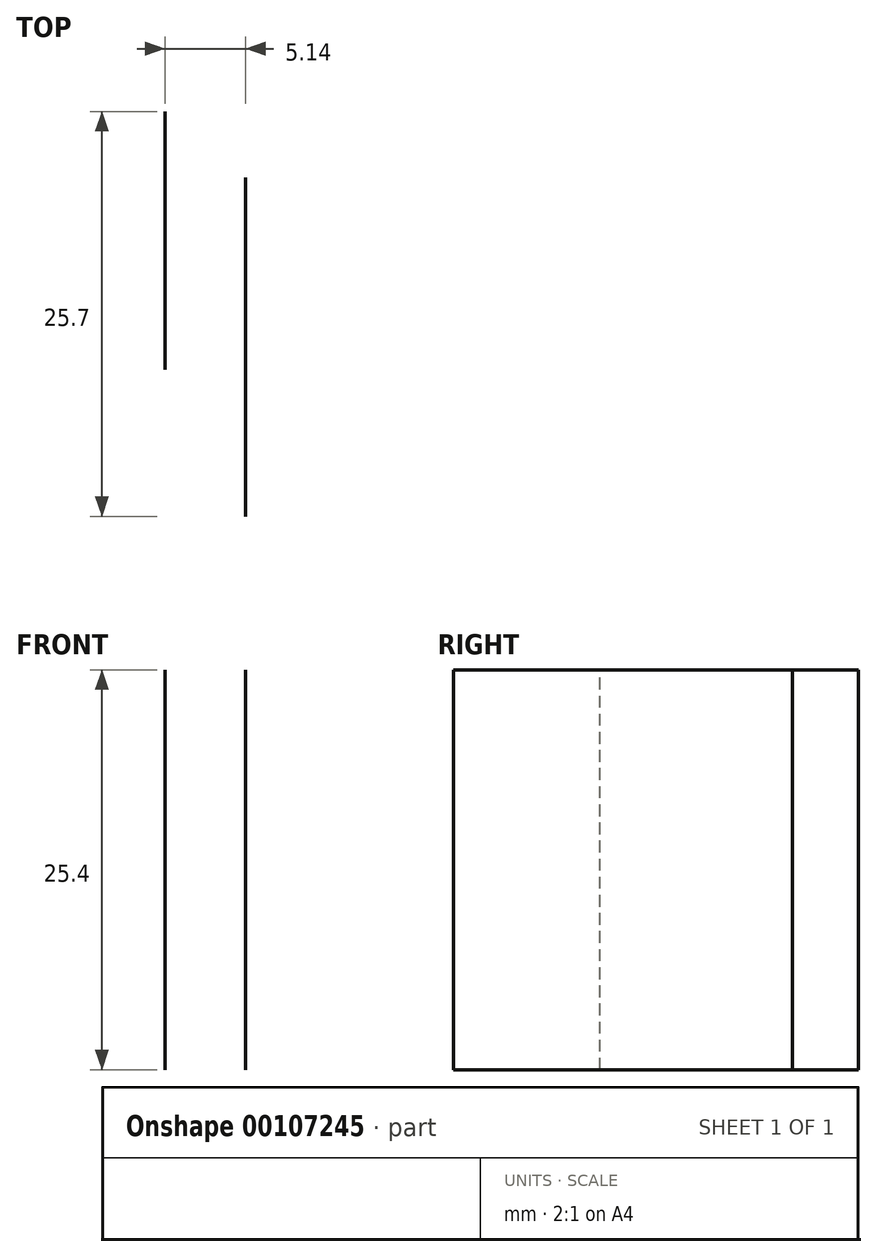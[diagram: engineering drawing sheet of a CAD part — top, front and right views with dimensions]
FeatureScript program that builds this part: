
annotation { "Feature Type Name" : "Feature", "Feature Type Description" : "" }
export const myFeature = defineFeature(function(context is Context, id is Id, definition is map)
    precondition{}
    {
        {
            var Q0;
            Q0=qCreatedBy(makeId("Top.planeOp"),FACE);
            var sketch = newSketch(context, id + "F0", { "sketchPlane" : qUnion([Q0])});
            skLineSegment(sketch, "E0.bottom", {"start": v(-113.75, 29.56) * mm, "end": v(112.79, 29.56) * mm});
            skLineSegment(sketch, "E0.top", {"start": v(-113.75, -33.42) * mm, "end": v(112.79, -33.42) * mm});
            skLineSegment(sketch, "E0.left", {"start": v(-113.75, 29.56) * mm, "end": v(-113.75, -33.42) * mm});
            skLineSegment(sketch, "E0.right", {"start": v(112.79, 29.56) * mm, "end": v(112.79, -33.42) * mm});
            skLineSegment(sketch, "E1", {"start": v(-27, 22.81) * mm, "end": v(-27, 6.43) * mm});
            skLineSegment(sketch, "E2", {"start": v(-21.85, 18.64) * mm, "end": v(-21.85, -2.9) * mm});
            skSolve(sketch);
        }
        {
            var Q0;
            Q0=qCreatedBy(makeId("Top.planeOp"),FACE);
            var sketch = newSketch(context, id + "F1", { "sketchPlane" : qUnion([Q0])});
            skLineSegment(sketch, "E3.0", {"start": v(-27, 22.81) * mm, "end": v(-27, 6.43) * mm});
            skLineSegment(sketch, "E4.0", {"start": v(-21.85, 18.64) * mm, "end": v(-21.85, -2.9) * mm});
            skLineSegment(sketch, "E5.1.0.0", {"start": v(-20.64, 22.81) * mm, "end": v(-20.64, 6.43) * mm});
            skLineSegment(sketch, "E5.direction1", {"start": v(-27, 6.43) * mm, "end": v(-20.64, 6.43) * mm, "construction": true});
            skLineSegment(sketch, "E6.0.3.0", {"start": v(-7.94, 22.81) * mm, "end": v(-7.94, 6.43) * mm});
            skLineSegment(sketch, "E6.0.5.0", {"start": v(4.76, 22.81) * mm, "end": v(4.76, 6.43) * mm});
            skLineSegment(sketch, "E6.0.9.0", {"start": v(30.16, 22.81) * mm, "end": v(30.16, 6.43) * mm});
            skLineSegment(sketch, "E6.0.11.0", {"start": v(42.86, 22.81) * mm, "end": v(42.86, 6.43) * mm});
            skLineSegment(sketch, "E7.1.0.0", {"start": v(40.15, 22.81) * mm, "end": v(40.15, -7.71) * mm});
            skLineSegment(sketch, "E7.1.0.1", {"start": v(47.85, 22.81) * mm, "end": v(47.85, 6.43) * mm});
            skLineSegment(sketch, "E7.2.0.0", {"start": v(83.24, 22.81) * mm, "end": v(83.24, -7.71) * mm});
            skLineSegment(sketch, "E7.2.0.1", {"start": v(90.95, 22.81) * mm, "end": v(90.95, 6.43) * mm});
            skLineSegment(sketch, "E7.direction1", {"start": v(-2.34, -7.71) * mm, "end": v(40.15, -7.71) * mm, "construction": true});
            skLineSegment(sketch, "E8.0.1.0", {"start": v(82.56, -42.65) * mm, "end": v(82.56, -73.17) * mm});
            skLineSegment(sketch, "E8.1.0.0", {"start": v(108.64, 22.81) * mm, "end": v(108.64, -7.71) * mm});
            skLineSegment(sketch, "E8.1.1.0", {"start": v(107.96, -42.65) * mm, "end": v(107.96, -73.17) * mm});
            skLineSegment(sketch, "E8.2.0.0", {"start": v(134.04, 22.81) * mm, "end": v(134.04, -7.71) * mm});
            skLineSegment(sketch, "E8.2.1.0", {"start": v(133.36, -42.65) * mm, "end": v(133.36, -73.17) * mm});
            skLineSegment(sketch, "E8.direction1", {"start": v(83.24, -7.71) * mm, "end": v(108.64, -7.71) * mm, "construction": true});
            skLineSegment(sketch, "E8.direction2", {"start": v(83.24, -7.71) * mm, "end": v(82.56, -73.17) * mm, "construction": true});
            skLineSegment(sketch, "E9", {"start": v(-34.4, 17.15) * mm, "end": v(-34.4, -7.9) * mm});
            skLineSegment(sketch, "E10", {"start": v(9.94, 19.4) * mm, "end": v(9.94, -5.66) * mm});
            skSolve(sketch);
        }
        {
            var Q0;
            Q0=sQuery(id+"F1.wireOp",EDGE,"E3.0");
            var Q1;
            Q1=sQuery(id+"F1.wireOp",EDGE,"E4.0");
            extrude(context, id + "F2", {"bodyType" : ToolBodyType.SURFACE, "surfaceEntities" : qUnion([Q0, Q1]), "depth" : 25.4 * mm});
        }
    });
